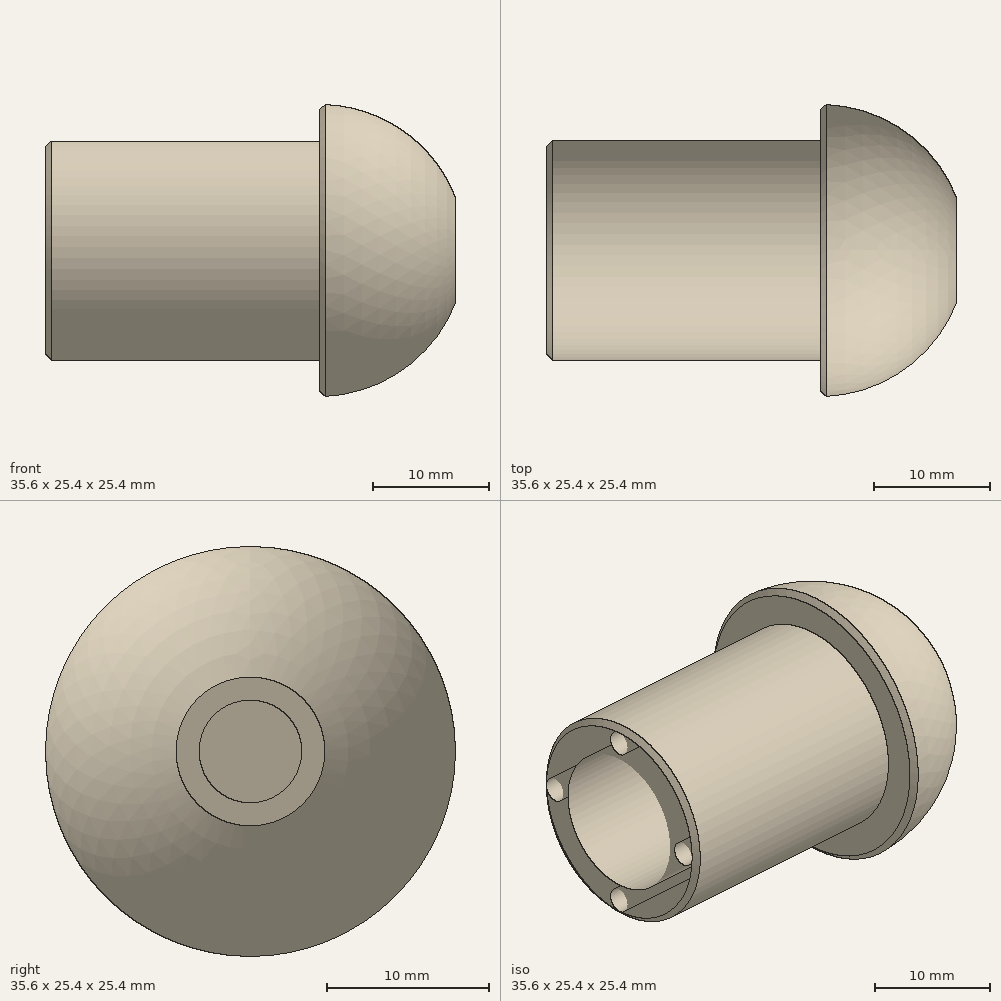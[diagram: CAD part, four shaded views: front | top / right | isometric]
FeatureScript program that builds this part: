
annotation { "Feature Type Name" : "Feature", "Feature Type Description" : "" }
export const myFeature = defineFeature(function(context is Context, id is Id, definition is map)
    precondition{}
    {
        {
            var Q0;
            Q0=qCreatedBy(makeId("Front.planeOp"),FACE);
            var sketch = newSketch(context, id + "F0", { "sketchPlane" : qUnion([Q0])});
            skLineSegment(sketch, "E0", {"start": v(-18.87, 0) * mm, "end": v(-6.1, 0) * mm});
            skLineSegment(sketch, "E1", {"start": v(0, 0) * mm, "end": v(0, 9.53) * mm});
            skLineSegment(sketch, "E2", {"start": v(0, 9.53) * mm, "end": v(23.81, 9.53) * mm});
            skLineSegment(sketch, "E3", {"start": v(23.81, 9.53) * mm, "end": v(23.81, 12.7) * mm});
            skPoint(sketch, "E4.centerSnap0", {"position": v(23.81, 11.11) * mm});
            skPoint(sketch, "E5.middle", {"position": v(39.41, 0) * mm});
            skLineSegment(sketch, "E6", {"start": v(36.28, 2.4) * mm, "end": v(36.28, 0) * mm});
            skLineSegment(sketch, "E7", {"start": v(36.28, 0) * mm, "end": v(0, 0) * mm});
            skArc(sketch, "E8", {"start": v(23.81, 12.7) * mm, "mid": v(31.9, 9.8) * mm, "end": v(36.28, 2.4) * mm});
            skSolve(sketch);
        }
        {
            var Q0;
            Q0=makeQuery(id+"F0.imprint","IMPRINT",FACE,{"disambiguationData":[TD([[makeQuery(id+"F0.imprint","IMPRINT",EDGE,{"derivedFrom":sQuery(id+"F0.wireOp",EDGE,"E1")}),-1.0]])]});
            var Q1;
            Q1=sQuery(id+"F0.wireOp",EDGE,"E7");
            revolve(context, id + "F1", {"entities" : qUnion([Q0]), "axis" : qUnion([Q1]), "revolveType" : RevolveType.FULL});
        }
        {
            var Q0;
            Q0=makeQuery(id+"F1.opRevolve","SWEPT_FACE",FACE,{"disambiguationData":[OSD([sQuery(id+"F0.wireOp",EDGE,"E6")])]});
            var sketch = newSketch(context, id + "F2", { "sketchPlane" : qUnion([Q0])});
            skCircle(sketch, "E9", {"center": v(0, 0) * mm, "radius": 3.18 * mm});
            skSolve(sketch);
        }
        {
            var Q0;
            Q0=qSketchRegion(id+"F2",true);
            extrude(context, id + "F3", {"entities" : qUnion([Q0]), "operationType" : NewBodyOperationType.REMOVE, "oppositeDirection" : true, "depth" : 15.24 * mm});
        }
        {
            var Q0;
            Q0=makeQuery(id+"F3.boolean.opBoolean","COPY",FACE,{"derivedFrom":makeQuery(id+"F3.opExtrude","CAP_FACE",FACE,{"disambiguationData":[OSD([sQuery(id+"F2.wireOp",EDGE,"E9")])],"isStart":false})});
            cPlane(context, id + "F4", {"entities" : qUnion([Q0]), "cplaneType" : CPlaneType.OFFSET, "offset" : 15.24 * mm, "width" : 152.4 * mm, "height" : 152.4 * mm});
        }
        {
            var Q0;
            Q0=qCreatedBy(id+"F4.planeOp",FACE);
            var sketch = newSketch(context, id + "F5", { "sketchPlane" : qUnion([Q0])});
            skCircle(sketch, "E10", {"center": v(0, 0) * mm, "radius": 4.76 * mm});
            skSolve(sketch);
        }
        {
            var Q0;
            Q0=qSketchRegion(id+"F5",true);
            extrude(context, id + "F6", {"entities" : qUnion([Q0]), "operationType" : NewBodyOperationType.REMOVE, "oppositeDirection" : true, "depth" : 0.64 * mm});
        }
        {
            var Q0;
            Q0=makeQuery(id+"F1.opRevolve","SWEPT_FACE",FACE,{"disambiguationData":[OSD([sQuery(id+"F0.wireOp",EDGE,"E1")])]});
            var sketch = newSketch(context, id + "F7", { "sketchPlane" : qUnion([Q0])});
            skCircle(sketch, "E11", {"center": v(0, 0) * mm, "radius": 6.35 * mm});
            skSolve(sketch);
        }
        {
            var Q0;
            Q0=qSketchRegion(id+"F7",true);
            extrude(context, id + "F8", {"entities" : qUnion([Q0]), "operationType" : NewBodyOperationType.REMOVE, "oppositeDirection" : true, "depth" : 19.05 * mm});
        }
        {
            var Q0;
            Q0=makeQuery(id+"F1.opRevolve","SWEPT_EDGE",EDGE,{"disambiguationData":[OSD([sQuery(id+"F0.wireOp",EDGE,"E3"),sQuery(id+"F0.wireOp",EDGE,"E8")])]});
            var Q1;
            Q1=makeQuery(id+"F1.opRevolve","SWEPT_EDGE",EDGE,{"disambiguationData":[OSD([sQuery(id+"F0.wireOp",EDGE,"E1"),sQuery(id+"F0.wireOp",EDGE,"E2")])]});
            chamfer(context, id + "F9", {"entities" : qUnion([Q0, Q1]), "width" : 0.5 * mm, "tangentPropagation" : true});
        }
        {
            var Q0;
            Q0=makeQuery(id+"F1.opRevolve","SWEPT_FACE",FACE,{"disambiguationData":[OSD([sQuery(id+"F0.wireOp",EDGE,"E1")])]});
            var sketch = newSketch(context, id + "F10", { "sketchPlane" : qUnion([Q0])});
            skCircle(sketch, "E12", {"center": v(0, 7.94) * mm, "radius": 1.08 * mm});
            skCircle(sketch, "E13", {"center": v(0, -7.94) * mm, "radius": 1.08 * mm});
            skCircle(sketch, "E14", {"center": v(7.94, 0) * mm, "radius": 1.08 * mm});
            skCircle(sketch, "E15", {"center": v(-7.94, 0) * mm, "radius": 1.08 * mm});
            skSolve(sketch);
        }
        {
            var Q0;
            Q0=qSketchRegion(id+"F10",true);
            extrude(context, id + "F11", {"entities" : qUnion([Q0]), "operationType" : NewBodyOperationType.REMOVE, "oppositeDirection" : true, "depth" : 9.52 * mm});
        }
    });
